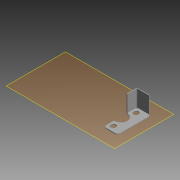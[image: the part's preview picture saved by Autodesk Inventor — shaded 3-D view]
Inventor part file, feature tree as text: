
AUTODESK INVENTOR PART (.ipt)
format: ipt  version: 2015 (Build 190159000, 159)  size: 164,352 bytes
history: native  units: mm
features: sheet_metal_op x10, sketch x4, other x4, reference x3, plane x1, hole x1
ambient origin geometry x8: Origin, YZ Plane, XZ Plane, XY Plane, X Axis, Y Axis, Z Axis, Center Point
bodies: Solid1 (feature_tree)
feature tree (23):
  plane  "Work Plane1"
  sheet_metal_op  "Face1"
  sheet_metal_op  "Flange1"
  sheet_metal_op  "Flange2"
  hole  "Hole1"  [1 undecoded]
  sheet_metal_op  "Flange3"
  sketch  "Sketch1"  dims[d0=10.0mm d2=1.0mm]
  reference  "Reference1"
  reference  "Reference2"
  reference  "Reference3"
  other  "Plate1"
  sketch  "Sketch2"  dims[d3=1.0mm]
  other  "Plate2"
  sheet_metal_op  "Bend1"
  sheet_metal_op  "Corner1"
  sketch  "Sketch3"  dims[d4=0.5mm]
  other  "Plate3"
  sheet_metal_op  "Bend2"
  sheet_metal_op  "Corner2"
  sketch  "Sketch4"  dims[d5=2.0mm d6=1.0mm d7=15.0mm d8=90.0deg d9=1.0mm d10=4.0mm d11=1.0mm d12=1.0mm d13=1.0mm d14=0.5mm d15=2.0mm d16=1.0mm d17=10.0mm d18=90.0deg d19=1.0mm d20=4.0mm d21=1.0mm d22=1.0mm d23=4.0mm d24=4.0mm d25=3.0mm d26=6.0mm d27=4.0mm d28=2.0mm d29=90.0deg d30=1.0mm d31=20.594885mm d32=12.0mm d33=1.0mm d34=0.5mm d35=2.0mm d36=1.0mm d37=1.0mm d38=0.0mm d39=1.0mm d40=4.0mm d41=1.0mm d42=1.0mm]
  other  "Plate4"
  sheet_metal_op  "Bend3"
  sheet_metal_op  "Corner3"
note: 1 required parameter value undecoded (feature->parameter linkage not recoverable at this tier; creation-order binding heuristic only, values carry confidence <= 0.55)
